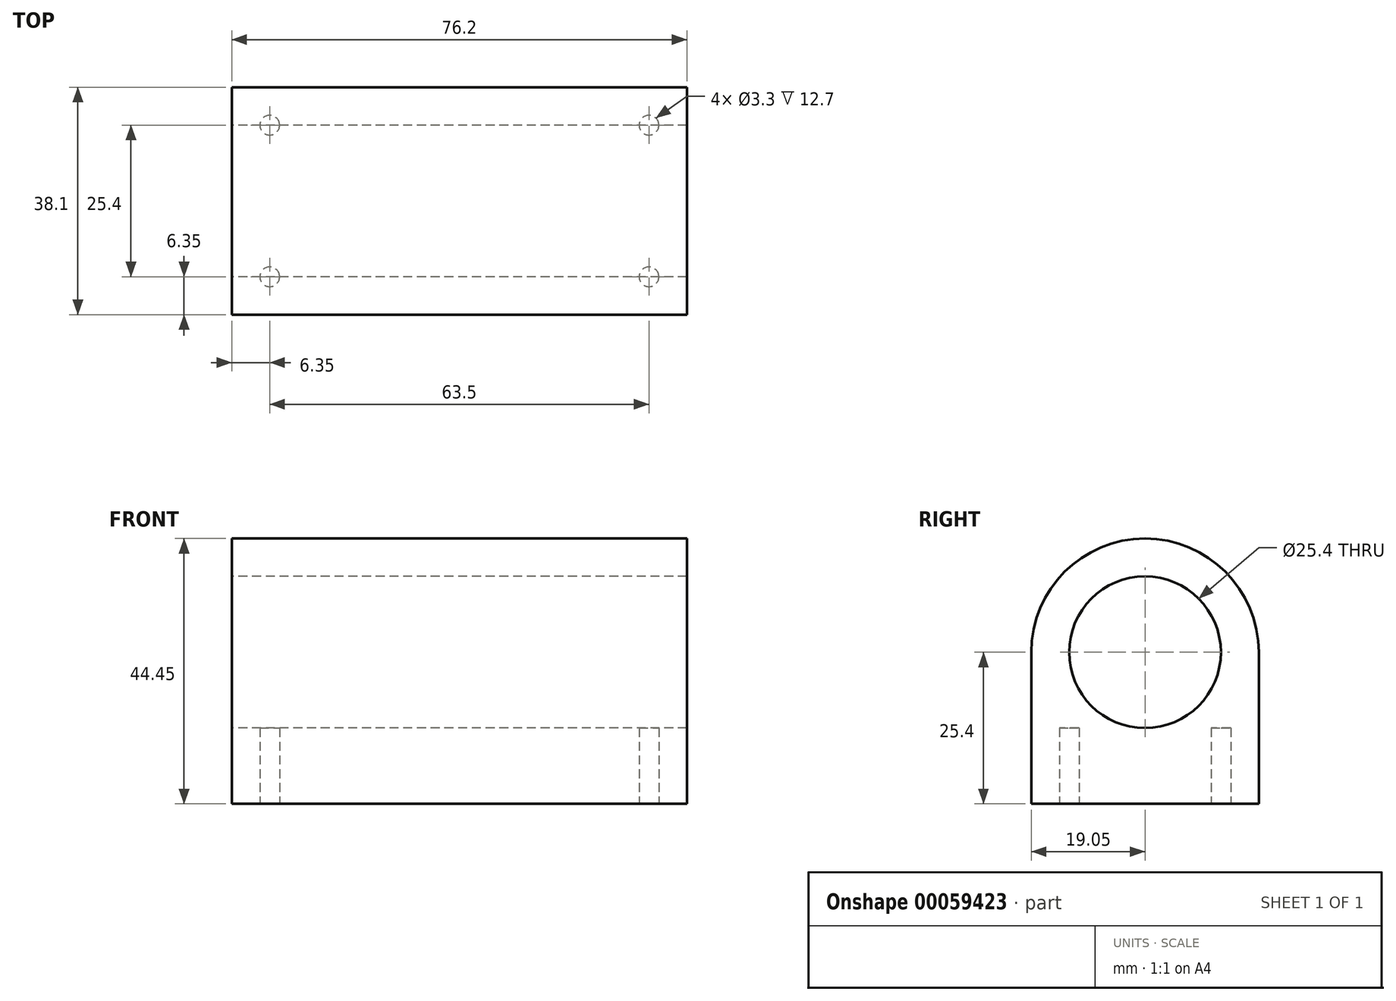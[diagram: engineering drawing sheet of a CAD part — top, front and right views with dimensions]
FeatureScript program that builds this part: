
annotation { "Feature Type Name" : "Feature", "Feature Type Description" : "" }
export const myFeature = defineFeature(function(context is Context, id is Id, definition is map)
    precondition{}
    {
        {
            var Q0;
            Q0=qCreatedBy(makeId("Right.planeOp"),FACE);
            var sketch = newSketch(context, id + "F0", { "sketchPlane" : qUnion([Q0])});
            skArc(sketch, "E0", {"start": v(19.05, 0) * mm, "mid": v(0, 19.05) * mm, "end": v(-19.05, 0) * mm});
            skLineSegment(sketch, "E1", {"start": v(-19.05, 0) * mm, "end": v(-19.05, -25.4) * mm});
            skLineSegment(sketch, "E2", {"start": v(-19.05, -25.4) * mm, "end": v(19.05, -25.4) * mm});
            skLineSegment(sketch, "E3", {"start": v(19.05, 0) * mm, "end": v(19.05, -25.4) * mm});
            skCircle(sketch, "E4", {"center": v(0, 0) * mm, "radius": 12.7 * mm});
            skSolve(sketch);
        }
        {
            var Q0;
            Q0=makeQuery(id+"F0.imprint","IMPRINT",FACE,{"disambiguationData":[TD([[makeQuery(id+"F0.imprint","IMPRINT",EDGE,{"derivedFrom":sQuery(id+"F0.wireOp",EDGE,"E0")}),1.0]])]});
            extrude(context, id + "F1", {"entities" : qUnion([Q0]), "endBound" : BoundingType.SYMMETRIC, "depth" : 76.2 * mm});
        }
        {
            var Q0;
            Q0=makeQuery(id+"F1.opExtrude","SWEPT_FACE",FACE,{"disambiguationData":[OSD([sQuery(id+"F0.wireOp",EDGE,"E2")])]});
            var sketch = newSketch(context, id + "F2", { "sketchPlane" : qUnion([Q0])});
            skCircle(sketch, "E5", {"center": v(-31.75, 12.7) * mm, "radius": 1.65 * mm});
            skCircle(sketch, "E6", {"center": v(-31.75, -12.7) * mm, "radius": 1.65 * mm});
            skCircle(sketch, "E7", {"center": v(31.75, -12.7) * mm, "radius": 1.65 * mm});
            skCircle(sketch, "E8", {"center": v(31.75, 12.7) * mm, "radius": 1.65 * mm});
            skSolve(sketch);
        }
        {
            var Q0;
            Q0=makeQuery(id+"F2.imprint","IMPRINT",FACE,{"disambiguationData":[TD([[makeQuery(id+"F2.imprint","IMPRINT",EDGE,{"derivedFrom":sQuery(id+"F2.wireOp",EDGE,"E5")}),1.0]])]});
            var Q1;
            Q1=makeQuery(id+"F2.imprint","IMPRINT",FACE,{"disambiguationData":[TD([[makeQuery(id+"F2.imprint","IMPRINT",EDGE,{"derivedFrom":sQuery(id+"F2.wireOp",EDGE,"E6")}),1.0]])]});
            var Q2;
            Q2=makeQuery(id+"F2.imprint","IMPRINT",FACE,{"disambiguationData":[TD([[makeQuery(id+"F2.imprint","IMPRINT",EDGE,{"derivedFrom":sQuery(id+"F2.wireOp",EDGE,"E8")}),1.0]])]});
            var Q3;
            Q3=makeQuery(id+"F2.imprint","IMPRINT",FACE,{"disambiguationData":[TD([[makeQuery(id+"F2.imprint","IMPRINT",EDGE,{"derivedFrom":sQuery(id+"F2.wireOp",EDGE,"E7")}),1.0]])]});
            extrude(context, id + "F3", {"entities" : qUnion([Q0, Q1, Q2, Q3]), "operationType" : NewBodyOperationType.REMOVE, "oppositeDirection" : true, "depth" : 12.7 * mm});
        }
    });
